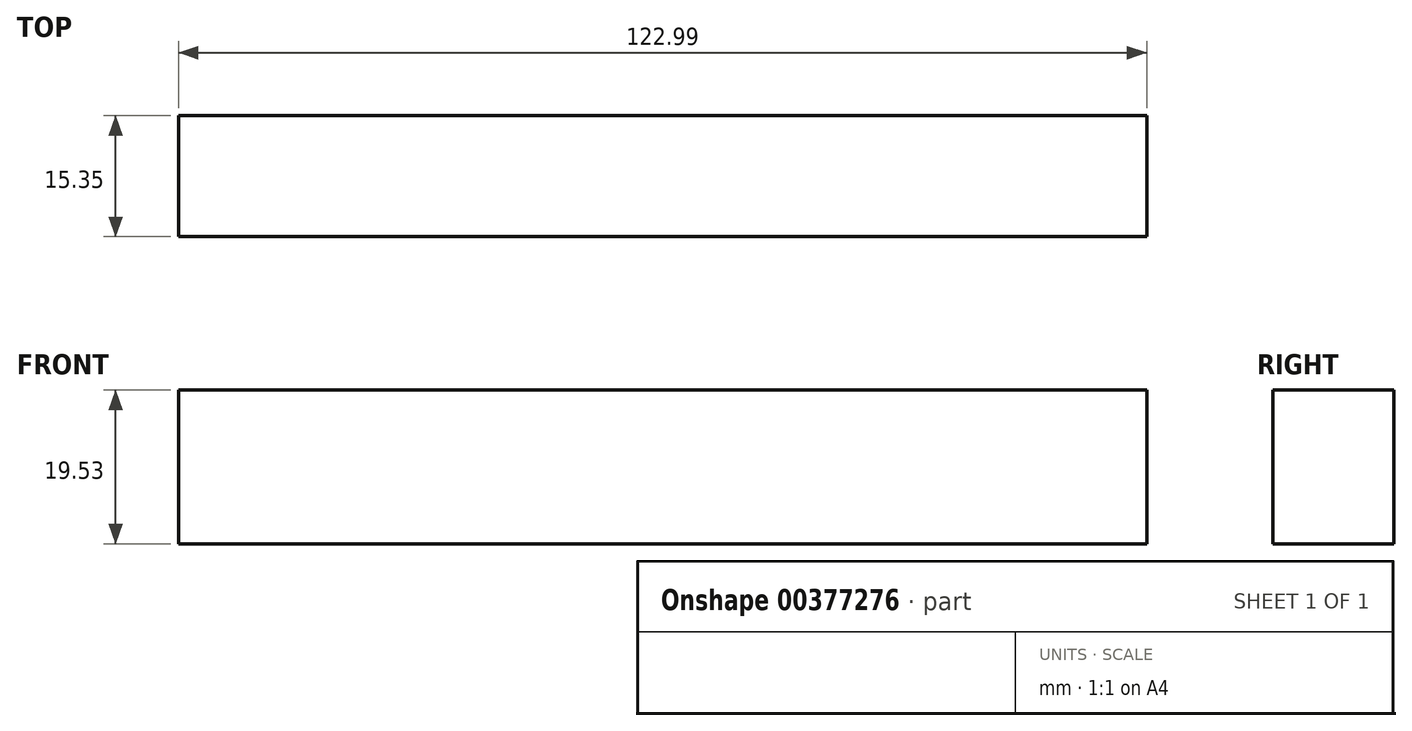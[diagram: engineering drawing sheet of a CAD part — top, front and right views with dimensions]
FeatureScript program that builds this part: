
annotation { "Feature Type Name" : "Feature", "Feature Type Description" : "" }
export const myFeature = defineFeature(function(context is Context, id is Id, definition is map)
    precondition{}
    {
        {
            var Q0;
            Q0=qCreatedBy(makeId("Front.planeOp"),FACE);
            var sketch = newSketch(context, id + "F0", { "sketchPlane" : qUnion([Q0])});
            skLineSegment(sketch, "E0.bottom", {"start": v(-63.5, 19.53) * mm, "end": v(59.49, 19.53) * mm});
            skLineSegment(sketch, "E0.top", {"start": v(-63.5, 0) * mm, "end": v(59.49, 0) * mm});
            skLineSegment(sketch, "E0.left", {"start": v(-63.5, 19.53) * mm, "end": v(-63.5, 0) * mm});
            skLineSegment(sketch, "E0.right", {"start": v(59.49, 19.53) * mm, "end": v(59.49, 0) * mm});
            skSolve(sketch);
        }
        {
            var Q0;
            Q0=makeQuery(id+"F0.imprint","IMPRINT",FACE,{"disambiguationData":[TD([[makeQuery(id+"F0.imprint","IMPRINT",EDGE,{"derivedFrom":sQuery(id+"F0.wireOp",EDGE,"E0.bottom")}),-1.0]])]});
            extrude(context, id + "F1", {"entities" : qUnion([Q0]), "depth" : 15.35 * mm});
        }
    });
